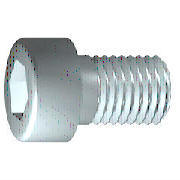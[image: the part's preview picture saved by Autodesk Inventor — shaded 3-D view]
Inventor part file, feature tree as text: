
AUTODESK INVENTOR PART (.ipt)
format: ipt  version: 2022 (Build 260153000, 153)  size: 196,608 bytes
history: native  units: mm (DEFAULTED — no unit token found)
features: sketch x2, other x1, extrude x1, plane x1, fillet x1
ambient origin geometry x7: Origin, YZ Plane, XY Plane, X Axis, Y Axis, Z Axis, Center Point
bodies: Solid1 (feature_tree)
feature tree (6):
  other  "Cuerpo"
  extrude  "Ranura"  Depth=3.0mm
  plane  "Work Plane1"
  fillet  "Fillet2"  Radius=3.0mm
  sketch  "Boceto1"  dims[d1=4.75mm d2=0.306825mm d3=3.0mm]
  sketch  "Boceto2"  dims[d4=1.3mm d5=60.0deg d6=3.0mm d7=3.0mm d8=2.886751mm d9=5.5mm d10=90.0deg d11=10.0mm d12=0.0mm d13=4.75mm d14=0.0mm d15=0.306725mm d16=0.306725mm d17=0.3mm d19=0.0mm d26=6.0mm d27=45.0deg d28=0.0mm d29=0.0mm d30=0.1mm]
